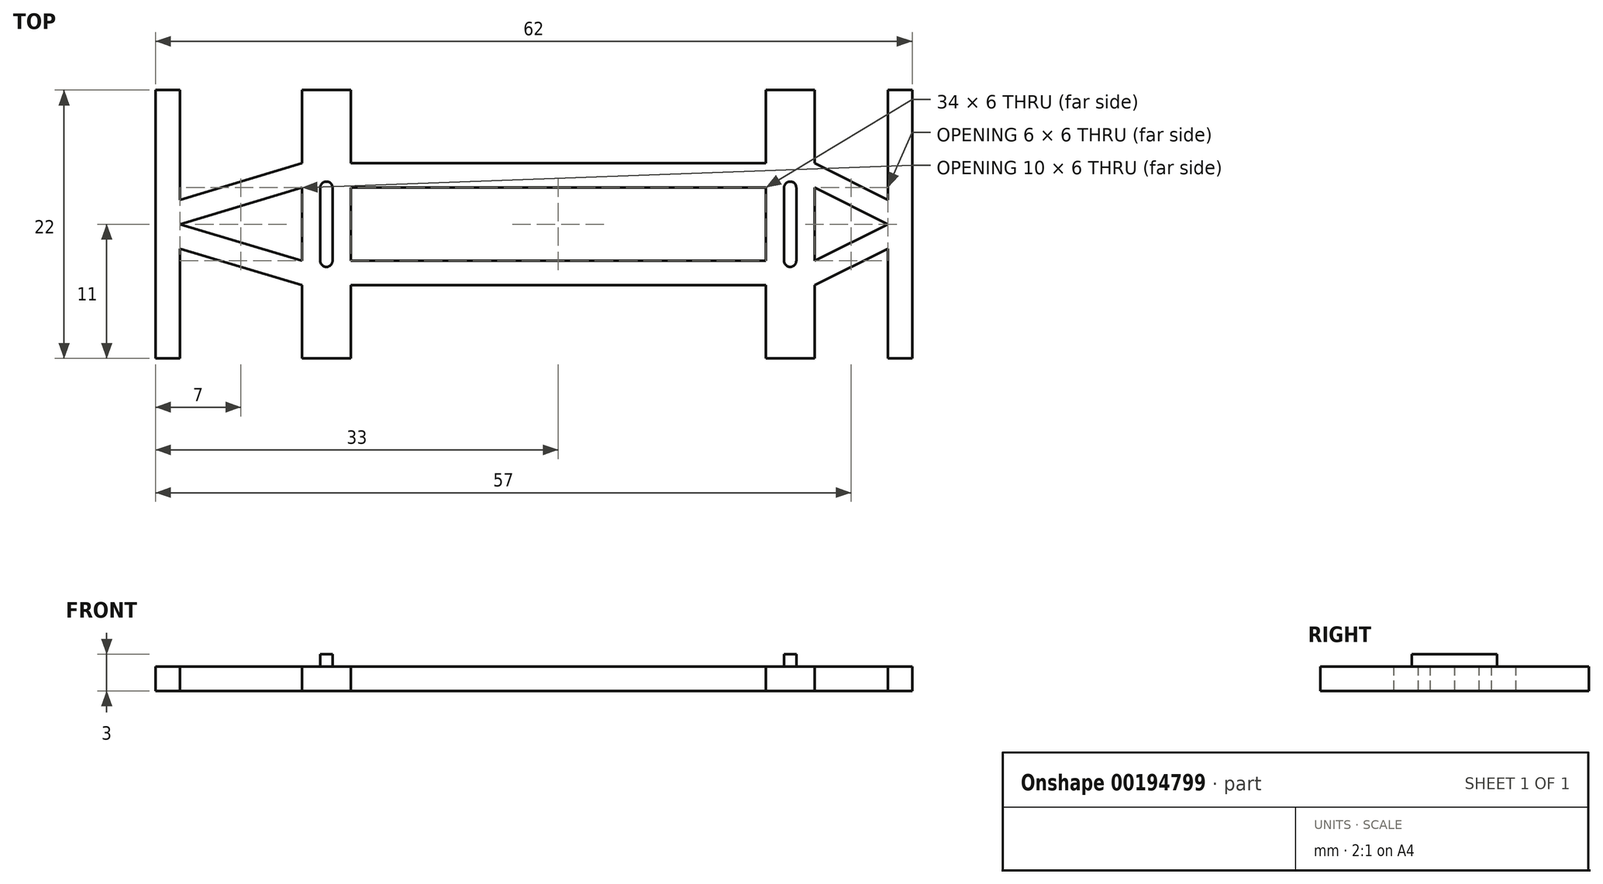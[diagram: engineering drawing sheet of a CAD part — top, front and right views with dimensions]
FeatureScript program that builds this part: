
annotation { "Feature Type Name" : "Feature", "Feature Type Description" : "" }
export const myFeature = defineFeature(function(context is Context, id is Id, definition is map)
    precondition{}
    {
        {
            var Q0;
            Q0=qCreatedBy(makeId("Top.planeOp"),FACE);
            var sketch = newSketch(context, id + "F0", { "sketchPlane" : qUnion([Q0])});
            skLineSegment(sketch, "E0", {"start": v(-17.03, 11) * mm, "end": v(111.77, 11) * mm, "construction": true});
            skLineSegment(sketch, "E1", {"start": v(0, 11) * mm, "end": v(0, 0) * mm});
            skLineSegment(sketch, "E2", {"start": v(0, 0) * mm, "end": v(2, 0) * mm});
            skLineSegment(sketch, "E3", {"start": v(2, 0) * mm, "end": v(2, 9) * mm});
            skLineSegment(sketch, "E4", {"start": v(2, 9) * mm, "end": v(12, 6) * mm});
            skLineSegment(sketch, "E5", {"start": v(12, 6) * mm, "end": v(12, 0) * mm});
            skLineSegment(sketch, "E6", {"start": v(12, 0) * mm, "end": v(16, 0) * mm});
            skLineSegment(sketch, "E7", {"start": v(16, 0) * mm, "end": v(16, 6) * mm});
            skLineSegment(sketch, "E8", {"start": v(16, 6) * mm, "end": v(50, 6) * mm});
            skLineSegment(sketch, "E9", {"start": v(50, 6) * mm, "end": v(50, 0) * mm});
            skLineSegment(sketch, "E10", {"start": v(50, 0) * mm, "end": v(54, 0) * mm});
            skLineSegment(sketch, "E11", {"start": v(54, 0) * mm, "end": v(54, 6) * mm});
            skLineSegment(sketch, "E12", {"start": v(54, 6) * mm, "end": v(60, 9) * mm});
            skLineSegment(sketch, "E13", {"start": v(60, 9) * mm, "end": v(60, 0) * mm});
            skLineSegment(sketch, "E14", {"start": v(60, 0) * mm, "end": v(62, 0) * mm});
            skLineSegment(sketch, "E15", {"start": v(62, 0) * mm, "end": v(62, 11) * mm});
            skLineSegment(sketch, "E16", {"start": v(2, 11) * mm, "end": v(12, 8) * mm});
            skLineSegment(sketch, "E17", {"start": v(16, 8) * mm, "end": v(50, 8) * mm});
            skLineSegment(sketch, "E18", {"start": v(54, 8) * mm, "end": v(60, 11) * mm});
            skLineSegment(sketch, "E19", {"start": v(50, 8) * mm, "end": v(50, 11) * mm});
            skLineSegment(sketch, "E20", {"start": v(16, 8) * mm, "end": v(16, 11) * mm});
            skLineSegment(sketch, "E21", {"start": v(12, 8) * mm, "end": v(12, 11) * mm});
            skLineSegment(sketch, "E22", {"start": v(54, 8) * mm, "end": v(54, 11) * mm});
            skLineSegment(sketch, "E23.MirrorCS", {"start": v(60, 22) * mm, "end": v(62, 22) * mm});
            skLineSegment(sketch, "E24.MirrorCS", {"start": v(0, 22) * mm, "end": v(2, 22) * mm});
            skLineSegment(sketch, "E25.MirrorCS", {"start": v(16, 14) * mm, "end": v(50, 14) * mm});
            skLineSegment(sketch, "E26.MirrorCS", {"start": v(60, 13) * mm, "end": v(60, 22) * mm});
            skLineSegment(sketch, "E27.MirrorCS", {"start": v(54, 16) * mm, "end": v(60, 13) * mm});
            skLineSegment(sketch, "E28.MirrorCS", {"start": v(54, 22) * mm, "end": v(54, 16) * mm});
            skLineSegment(sketch, "E29.MirrorCS", {"start": v(50, 22) * mm, "end": v(54, 22) * mm});
            skLineSegment(sketch, "E30.MirrorCS", {"start": v(50, 16) * mm, "end": v(50, 22) * mm});
            skLineSegment(sketch, "E31.MirrorCS", {"start": v(16, 16) * mm, "end": v(50, 16) * mm});
            skLineSegment(sketch, "E32.MirrorCS", {"start": v(16, 22) * mm, "end": v(16, 16) * mm});
            skLineSegment(sketch, "E33.MirrorCS", {"start": v(12, 22) * mm, "end": v(16, 22) * mm});
            skLineSegment(sketch, "E34.MirrorCS", {"start": v(12, 16) * mm, "end": v(12, 22) * mm});
            skLineSegment(sketch, "E35.MirrorCS", {"start": v(2, 13) * mm, "end": v(12, 16) * mm});
            skLineSegment(sketch, "E36.MirrorCS", {"start": v(2, 22) * mm, "end": v(2, 13) * mm});
            skLineSegment(sketch, "E37.MirrorCS", {"start": v(54, 14) * mm, "end": v(54, 11) * mm});
            skLineSegment(sketch, "E38.MirrorCS", {"start": v(16, 14) * mm, "end": v(16, 11) * mm});
            skLineSegment(sketch, "E39.MirrorCS", {"start": v(12, 14) * mm, "end": v(12, 11) * mm});
            skLineSegment(sketch, "E40.MirrorCS", {"start": v(50, 14) * mm, "end": v(50, 11) * mm});
            skLineSegment(sketch, "E41.MirrorCS", {"start": v(2, 11) * mm, "end": v(12, 14) * mm});
            skLineSegment(sketch, "E42.MirrorCS", {"start": v(0, 11) * mm, "end": v(0, 22) * mm});
            skLineSegment(sketch, "E43.MirrorCS", {"start": v(62, 22) * mm, "end": v(62, 11) * mm});
            skLineSegment(sketch, "E44.MirrorCS", {"start": v(54, 14) * mm, "end": v(60, 11) * mm});
            skSolve(sketch);
        }
        {
            var Q0;
            Q0 = qSketchRegion(id + "F0", true);
            extrude(context, id + "F1", {"entities" : qUnion([Q0]), "depth" : 2 * mm});
        }
        {
            var Q0;
            Q0=makeQuery(id+"F1.opExtrude","CAP_FACE",FACE,{"disambiguationData":[OSD([sQuery(id+"F0.wireOp",EDGE,"E1"),sQuery(id+"F0.wireOp",EDGE,"E2"),sQuery(id+"F0.wireOp",EDGE,"E3"),sQuery(id+"F0.wireOp",EDGE,"E4"),sQuery(id+"F0.wireOp",EDGE,"E5"),sQuery(id+"F0.wireOp",EDGE,"E6"),sQuery(id+"F0.wireOp",EDGE,"E7"),sQuery(id+"F0.wireOp",EDGE,"E8"),sQuery(id+"F0.wireOp",EDGE,"E9"),sQuery(id+"F0.wireOp",EDGE,"E10"),sQuery(id+"F0.wireOp",EDGE,"E11"),sQuery(id+"F0.wireOp",EDGE,"E12"),sQuery(id+"F0.wireOp",EDGE,"E13"),sQuery(id+"F0.wireOp",EDGE,"E14"),sQuery(id+"F0.wireOp",EDGE,"E15"),sQuery(id+"F0.wireOp",EDGE,"E16"),sQuery(id+"F0.wireOp",EDGE,"E17"),sQuery(id+"F0.wireOp",EDGE,"E18"),sQuery(id+"F0.wireOp",EDGE,"E19"),sQuery(id+"F0.wireOp",EDGE,"E20"),sQuery(id+"F0.wireOp",EDGE,"E21"),sQuery(id+"F0.wireOp",EDGE,"E22"),sQuery(id+"F0.wireOp",EDGE,"E23.MirrorCS"),sQuery(id+"F0.wireOp",EDGE,"E24.MirrorCS"),sQuery(id+"F0.wireOp",EDGE,"E25.MirrorCS"),sQuery(id+"F0.wireOp",EDGE,"E26.MirrorCS"),sQuery(id+"F0.wireOp",EDGE,"E27.MirrorCS"),sQuery(id+"F0.wireOp",EDGE,"E28.MirrorCS"),sQuery(id+"F0.wireOp",EDGE,"E29.MirrorCS"),sQuery(id+"F0.wireOp",EDGE,"E30.MirrorCS"),sQuery(id+"F0.wireOp",EDGE,"E31.MirrorCS"),sQuery(id+"F0.wireOp",EDGE,"E32.MirrorCS"),sQuery(id+"F0.wireOp",EDGE,"E33.MirrorCS"),sQuery(id+"F0.wireOp",EDGE,"E34.MirrorCS"),sQuery(id+"F0.wireOp",EDGE,"E35.MirrorCS"),sQuery(id+"F0.wireOp",EDGE,"E36.MirrorCS"),sQuery(id+"F0.wireOp",EDGE,"E37.MirrorCS"),sQuery(id+"F0.wireOp",EDGE,"E38.MirrorCS"),sQuery(id+"F0.wireOp",EDGE,"E39.MirrorCS"),sQuery(id+"F0.wireOp",EDGE,"E40.MirrorCS"),sQuery(id+"F0.wireOp",EDGE,"E41.MirrorCS"),sQuery(id+"F0.wireOp",EDGE,"E42.MirrorCS"),sQuery(id+"F0.wireOp",EDGE,"E43.MirrorCS"),sQuery(id+"F0.wireOp",EDGE,"E44.MirrorCS")])],"isStart":false});
            var sketch = newSketch(context, id + "F2", { "sketchPlane" : qUnion([Q0])});
            skLineSegment(sketch, "E45", {"start": v(14, 14) * mm, "end": v(14, 8) * mm, "construction": true});
            skArc(sketch, "E46", {"start": v(14.5, 14) * mm, "mid": v(14, 14.5) * mm, "end": v(13.5, 14) * mm});
            skArc(sketch, "E47", {"start": v(14.5, 8) * mm, "mid": v(14, 7.5) * mm, "end": v(13.5, 8) * mm});
            skLineSegment(sketch, "E48", {"start": v(13.5, 14) * mm, "end": v(13.5, 8) * mm});
            skLineSegment(sketch, "E49", {"start": v(14.5, 14) * mm, "end": v(14.5, 8) * mm});
            skLineSegment(sketch, "E50", {"start": v(14, 14) * mm, "end": v(16, 14) * mm, "construction": true});
            skLineSegment(sketch, "E51", {"start": v(33, 27.46) * mm, "end": v(33, 0.7) * mm, "construction": true});
            skPoint(sketch, "E51.startSnap0", {"position": v(33, 16) * mm});
            skArc(sketch, "E52.MirrorCS", {"start": v(51.5, 14) * mm, "mid": v(52, 14.5) * mm, "end": v(52.5, 14) * mm});
            skLineSegment(sketch, "E53.MirrorCS", {"start": v(52, 14) * mm, "end": v(50, 14) * mm, "construction": true});
            skLineSegment(sketch, "E54.MirrorCS", {"start": v(51.5, 14) * mm, "end": v(51.5, 8) * mm});
            skLineSegment(sketch, "E55.MirrorCS", {"start": v(52.5, 14) * mm, "end": v(52.5, 8) * mm});
            skLineSegment(sketch, "E56.MirrorCS", {"start": v(52, 14) * mm, "end": v(52, 8) * mm, "construction": true});
            skArc(sketch, "E57.MirrorCS", {"start": v(51.5, 8) * mm, "mid": v(52, 7.5) * mm, "end": v(52.5, 8) * mm});
            skSolve(sketch);
        }
        {
            var Q0;
            Q0 = qSketchRegion(id + "F2", true);
            extrude(context, id + "F3", {"entities" : qUnion([Q0]), "operationType" : NewBodyOperationType.ADD, "depth" : 1 * mm});
        }
    });
